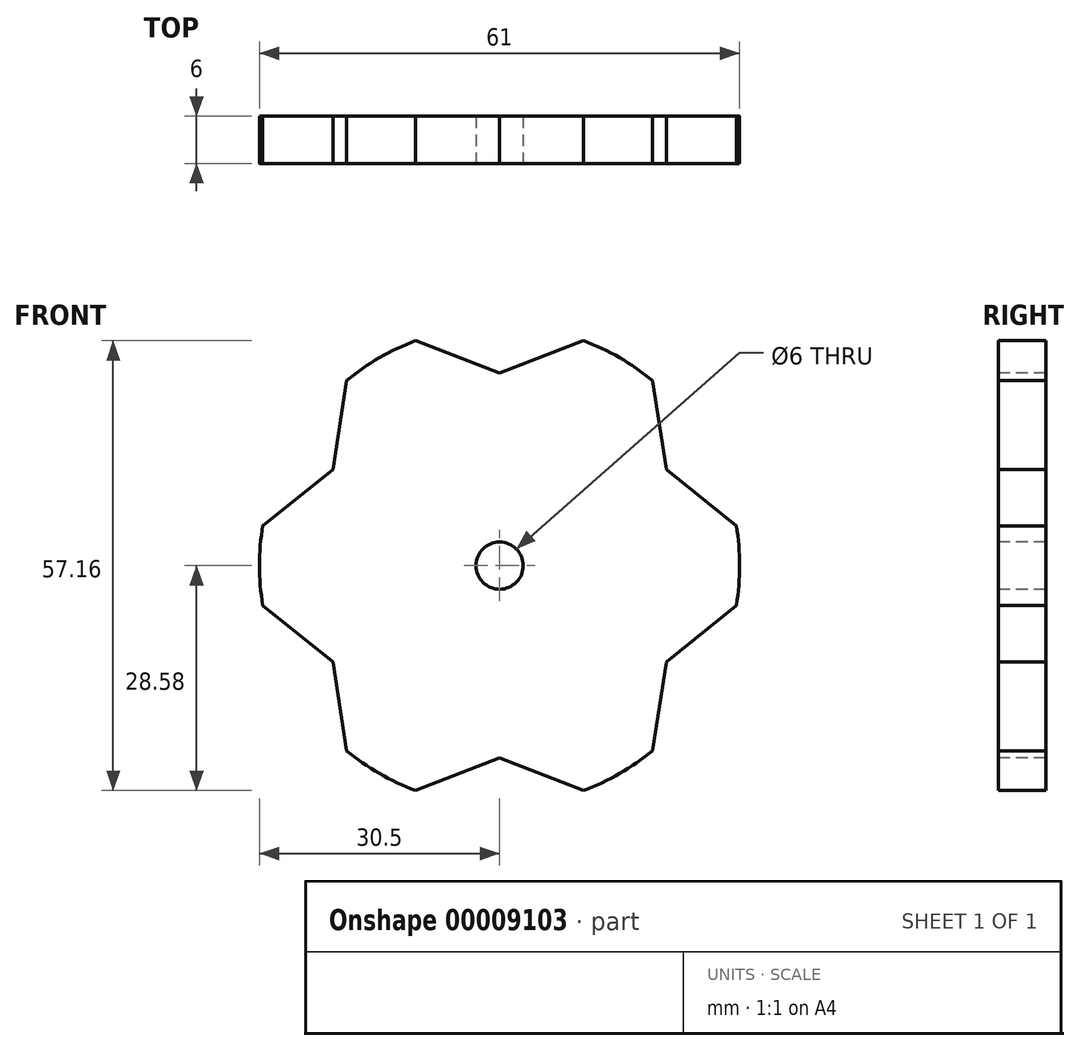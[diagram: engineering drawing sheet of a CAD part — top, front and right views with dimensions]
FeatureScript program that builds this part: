
annotation { "Feature Type Name" : "Feature", "Feature Type Description" : "" }
export const myFeature = defineFeature(function(context is Context, id is Id, definition is map)
    precondition{}
    {
        {
            var Q0;
            Q0=qCreatedBy(makeId("Front.planeOp"),FACE);
            var sketch = newSketch(context, id + "F0", { "sketchPlane" : qUnion([Q0])});
            skCircle(sketch, "E0", {"center": v(0, 0) * mm, "radius": 30.5 * mm});
            skSolve(sketch);
        }
        {
            var Q0;
            Q0 = qSketchRegion(id + "F0", true);
            extrude(context, id + "F1", {"entities" : qUnion([Q0]), "depth" : 6 * mm});
        }
        {
            var Q0;
            Q0=makeQuery(id+"F1.opExtrude","CAP_FACE",FACE,{"disambiguationData":[OSD([sQuery(id+"F0.wireOp",EDGE,"E0")])],"isStart":false});
            var sketch = newSketch(context, id + "F2", { "sketchPlane" : qUnion([Q0])});
            skLineSegment(sketch, "E1", {"start": v(0, 45.85) * mm, "end": v(0, 24.45) * mm});
            skLineSegment(sketch, "E2", {"start": v(0, 24.45) * mm, "end": v(29.95, 36.07) * mm});
            skLineSegment(sketch, "E3", {"start": v(29.95, 36.07) * mm, "end": v(0, 45.85) * mm});
            skLineSegment(sketch, "E4.MirrorCS", {"start": v(-29.95, 36.07) * mm, "end": v(0, 45.85) * mm});
            skLineSegment(sketch, "E5.MirrorCS", {"start": v(0, 24.45) * mm, "end": v(-29.95, 36.07) * mm});
            skLineSegment(sketch, "E6.1.0", {"start": v(-21.18, 12.23) * mm, "end": v(-16.26, 43.97) * mm});
            skLineSegment(sketch, "E6.1.1", {"start": v(-21.18, 12.23) * mm, "end": v(-46.2, -7.9) * mm});
            skLineSegment(sketch, "E6.2.0", {"start": v(-21.18, -12.23) * mm, "end": v(-46.2, 7.9) * mm});
            skLineSegment(sketch, "E6.2.1", {"start": v(-21.18, -12.23) * mm, "end": v(-16.26, -43.97) * mm});
            skLineSegment(sketch, "E6.3.0", {"start": v(0, -24.45) * mm, "end": v(-29.95, -36.07) * mm});
            skLineSegment(sketch, "E6.3.1", {"start": v(0, -24.45) * mm, "end": v(29.95, -36.07) * mm});
            skLineSegment(sketch, "E6.4.0", {"start": v(21.18, -12.23) * mm, "end": v(16.26, -43.97) * mm});
            skLineSegment(sketch, "E6.4.1", {"start": v(21.18, -12.23) * mm, "end": v(46.2, 7.9) * mm});
            skLineSegment(sketch, "E6.5.0", {"start": v(21.18, 12.23) * mm, "end": v(46.2, -7.9) * mm});
            skLineSegment(sketch, "E6.5.1", {"start": v(21.18, 12.23) * mm, "end": v(16.26, 43.97) * mm});
            skPoint(sketch, "E6.center", {"position": v(0, 0) * mm});
            skSolve(sketch);
        }
        {
            var Q0;
            {var subQ1=sQuery(id+"F2.wireOp",EDGE,"E6.1.1");var subQ3=sQuery(id+"F2.wireOp",EDGE,"E6.1.0");var subQ5=makeQuery(id+"F2.imprint","INTERSECT",VERTEX,{"derivedFrom":[subQ3,subQ1]});Q0=makeQuery(id+"F2.imprint","IMPRINT",FACE,{"disambiguationData":[TD([[makeQuery(id+"F2.imprint","IMPRINT",EDGE,{"disambiguationData":[TD([[subQ5,-1.0]])],"derivedFrom":subQ3}),1.0]])]});}
            var Q1;
            {var subQ1=sQuery(id+"F2.wireOp",EDGE,"E6.2.1");var subQ3=sQuery(id+"F2.wireOp",EDGE,"E6.2.0");var subQ5=makeQuery(id+"F2.imprint","INTERSECT",VERTEX,{"derivedFrom":[subQ3,subQ1]});Q1=makeQuery(id+"F2.imprint","IMPRINT",FACE,{"disambiguationData":[TD([[makeQuery(id+"F2.imprint","IMPRINT",EDGE,{"disambiguationData":[TD([[subQ5,-1.0]])],"derivedFrom":subQ3}),1.0]])]});}
            var Q2;
            {var subQ1=sQuery(id+"F2.wireOp",EDGE,"E6.3.1");var subQ3=sQuery(id+"F2.wireOp",EDGE,"E6.3.0");var subQ5=makeQuery(id+"F2.imprint","INTERSECT",VERTEX,{"derivedFrom":[subQ3,subQ1]});Q2=makeQuery(id+"F2.imprint","IMPRINT",FACE,{"disambiguationData":[TD([[makeQuery(id+"F2.imprint","IMPRINT",EDGE,{"disambiguationData":[TD([[subQ5,-1.0]])],"derivedFrom":subQ3}),1.0]])]});}
            var Q3;
            {var subQ1=sQuery(id+"F2.wireOp",EDGE,"E6.4.1");var subQ3=sQuery(id+"F2.wireOp",EDGE,"E6.4.0");var subQ5=makeQuery(id+"F2.imprint","INTERSECT",VERTEX,{"derivedFrom":[subQ3,subQ1]});Q3=makeQuery(id+"F2.imprint","IMPRINT",FACE,{"disambiguationData":[TD([[makeQuery(id+"F2.imprint","IMPRINT",EDGE,{"disambiguationData":[TD([[subQ5,-1.0]])],"derivedFrom":subQ3}),1.0]])]});}
            var Q4;
            {var subQ1=sQuery(id+"F2.wireOp",EDGE,"E6.5.1");var subQ3=sQuery(id+"F2.wireOp",EDGE,"E6.5.0");var subQ5=makeQuery(id+"F2.imprint","INTERSECT",VERTEX,{"derivedFrom":[subQ3,subQ1]});Q4=makeQuery(id+"F2.imprint","IMPRINT",FACE,{"disambiguationData":[TD([[makeQuery(id+"F2.imprint","IMPRINT",EDGE,{"disambiguationData":[TD([[subQ5,-1.0]])],"derivedFrom":subQ3}),1.0]])]});}
            var Q5;
            {var subQ0=makeQuery(id+"F1.opExtrude","CAP_EDGE",EDGE,{"disambiguationData":[OSD([sQuery(id+"F0.wireOp",EDGE,"E0")])],"isStart":false});var subQ3=sQuery(id+"F2.wireOp",EDGE,"E1");var subQ4=makeQuery(id+"F2.imprint","INTERSECT",VERTEX,{"derivedFrom":[subQ0,subQ3]});Q5=makeQuery(id+"F2.imprint","IMPRINT",FACE,{"disambiguationData":[TD([[makeQuery(id+"F2.imprint","IMPRINT",EDGE,{"disambiguationData":[TD([[subQ4,1.0]])],"derivedFrom":subQ0}),1.0]])]});}
            var Q6;
            {var subQ0=makeQuery(id+"F1.opExtrude","CAP_EDGE",EDGE,{"disambiguationData":[OSD([sQuery(id+"F0.wireOp",EDGE,"E0")])],"isStart":false});var subQ3=sQuery(id+"F2.wireOp",EDGE,"E1");var subQ4=makeQuery(id+"F2.imprint","INTERSECT",VERTEX,{"derivedFrom":[subQ0,subQ3]});Q6=makeQuery(id+"F2.imprint","IMPRINT",FACE,{"disambiguationData":[TD([[makeQuery(id+"F2.imprint","IMPRINT",EDGE,{"disambiguationData":[TD([[subQ4,-1.0]])],"derivedFrom":subQ0}),1.0]])]});}
            extrude(context, id + "F3", {"entities" : qUnion([Q0, Q1, Q2, Q3, Q4, Q5, Q6]), "operationType" : NewBodyOperationType.REMOVE, "endBound" : BoundingType.THROUGH_ALL, "oppositeDirection" : true, "depth" : 25 * mm});
        }
        {
            var Q0;
            Q0=makeQuery(id+"F1.opExtrude","CAP_FACE",FACE,{"disambiguationData":[OSD([sQuery(id+"F0.wireOp",EDGE,"E0")])],"isStart":false});
            var sketch = newSketch(context, id + "F4", { "sketchPlane" : qUnion([Q0])});
            skCircle(sketch, "E7", {"center": v(0, 0) * mm, "radius": 3 * mm});
            skSolve(sketch);
        }
        {
            var Q0;
            Q0 = qSketchRegion(id + "F4", true);
            extrude(context, id + "F5", {"entities" : qUnion([Q0]), "operationType" : NewBodyOperationType.REMOVE, "endBound" : BoundingType.THROUGH_ALL, "oppositeDirection" : true, "depth" : 25 * mm});
        }
    });
